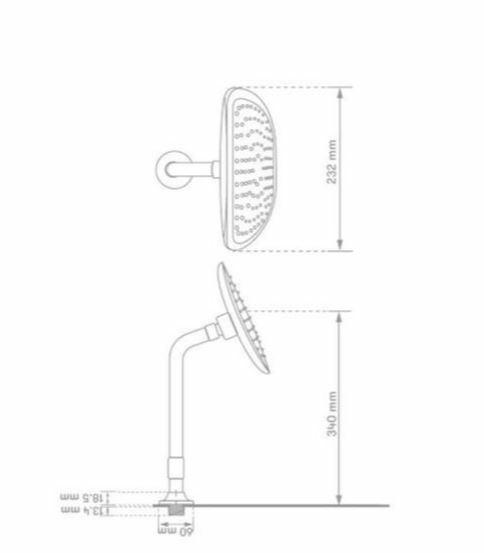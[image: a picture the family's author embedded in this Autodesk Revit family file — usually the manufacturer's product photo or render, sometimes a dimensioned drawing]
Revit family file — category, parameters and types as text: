
# Revit family: 01-1130-11 REGADERA MÓVIL PLÁSTICA
name_source: partatom
category: Plumbing Fixtures
revit_build: Autodesk Revit 2018 (Build: 20170223_1515(x64)
units: mm (PartAtom-declared; Revit-internal decimal feet)

## family parameters
Cut with Voids When Loaded = No
Host = Face
OmniClass Number = 23.31.11.00
Part Type = Normal
Room Calculation Point = No
Round Connector Dimension = Use Diameter
Shared = No

## types (1)
- 01-1130-11
    Alto = 118 mm
    Ancho = 60 mm  [stored 0.19685 ft]
    CW Connection = Yes
    Default Elevation = 0 mm  [stored 0 ft]
    Description = Regadera
    Finish = Plastico ABS Cromado
    HW Connection = Yes
    Link Ficha Tecnica = http://infotecnica.gricol.com
    Manufacturer = Gricol
    Model = 01-1130-11
    Product Name = REGADERA MÓVIL PLÁSTICA
    Profundidad = 150 mm
    Type Image = <None>
    URL = https://www.gricol.com
    Vent Connection = No
    Waste Connection = No

note: [stored X ft] marks values corroborated as IEEE doubles in the binary element streams (Revit-internal decimal feet)

## geometry (parser evidence)
native form markers: Blend x8, Sweep x13
no freeform markers — native parametric forms only
